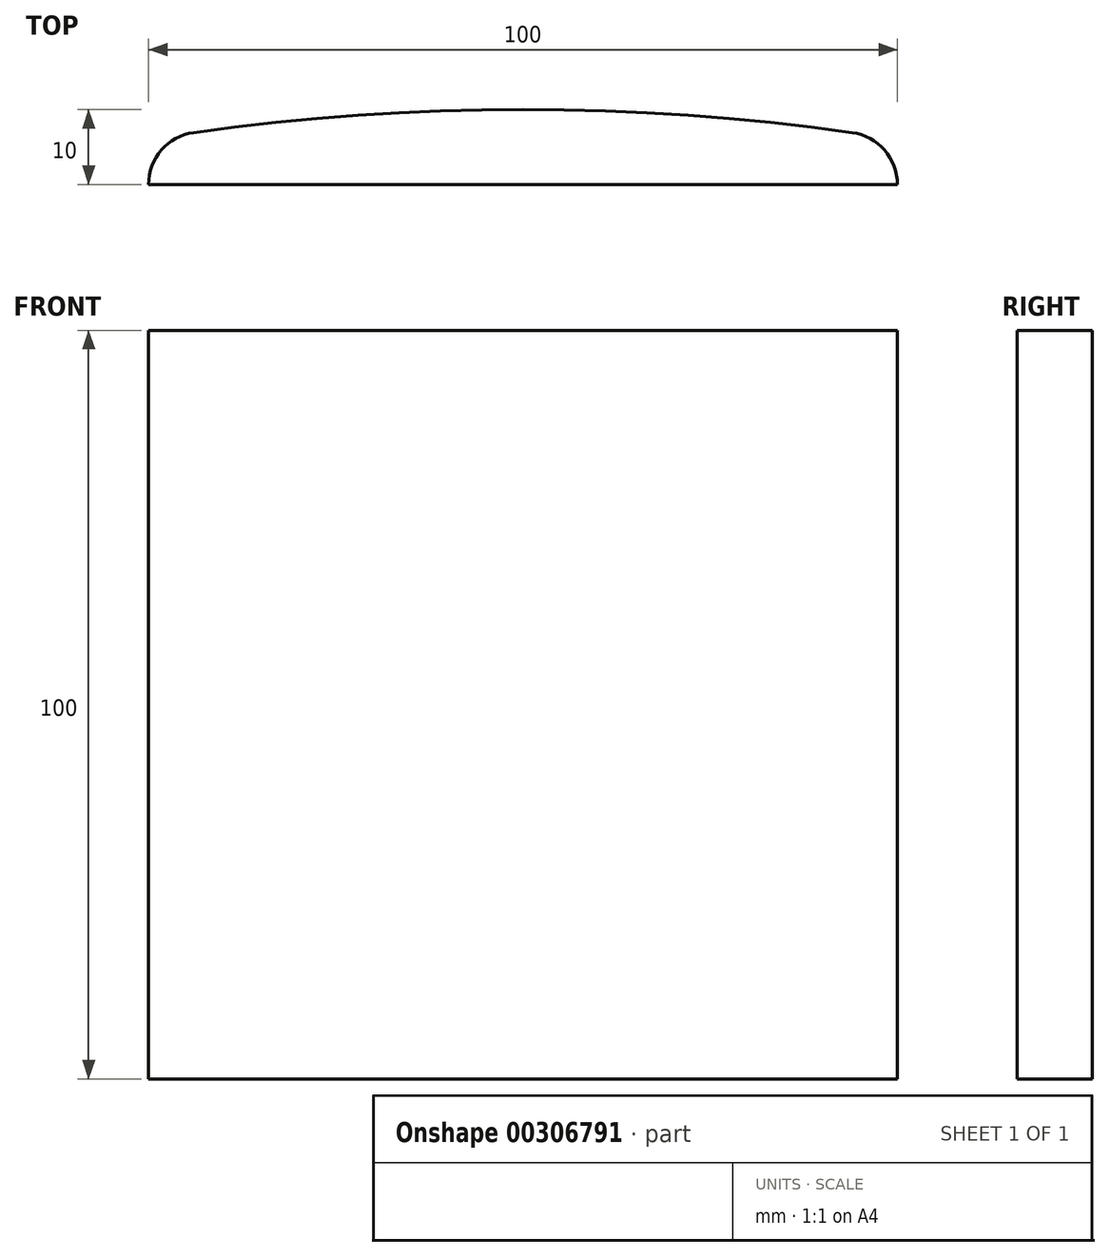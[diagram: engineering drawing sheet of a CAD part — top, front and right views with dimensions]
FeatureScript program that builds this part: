
annotation { "Feature Type Name" : "Feature", "Feature Type Description" : "" }
export const myFeature = defineFeature(function(context is Context, id is Id, definition is map)
    precondition{}
    {
        {
            var Q0;
            Q0=qCreatedBy(makeId("Top.planeOp"),FACE);
            var sketch = newSketch(context, id + "F0", { "sketchPlane" : qUnion([Q0])});
            skArc(sketch, "E0", {"start": v(100, 0) * mm, "mid": v(50, 2.63) * mm, "end": v(0, 0) * mm, "construction": true});
            skLineSegment(sketch, "E1.bottom", {"start": v(0, 0) * mm, "end": v(100, 0) * mm});
            skLineSegment(sketch, "E1.top", {"start": v(7, 7) * mm, "end": v(93, 7) * mm, "construction": true});
            skLineSegment(sketch, "E1.left", {"start": v(0, 0) * mm, "end": v(0, 0) * mm});
            skLineSegment(sketch, "E1.right", {"start": v(100, 0) * mm, "end": v(100, 0) * mm});
            skPoint(sketch, "E2.visualSharp", {"position": v(0, 7) * mm});
            skArc(sketch, "E2.filletArc", {"start": v(7, 7) * mm, "mid": v(2.05, 4.95) * mm, "end": v(0, 0) * mm});
            skPoint(sketch, "E3.visualSharp", {"position": v(100, 7) * mm});
            skArc(sketch, "E3.filletArc", {"start": v(100, 0) * mm, "mid": v(97.95, 4.95) * mm, "end": v(93, 7) * mm});
            skArc(sketch, "E4", {"start": v(93.97, 6.93) * mm, "mid": v(50, 10) * mm, "end": v(6.03, 6.93) * mm});
            skSolve(sketch);
        }
        {
            var Q0;
            {var subQ0=sQuery(id+"F0.wireOp",EDGE,"E1.bottom");Q0=makeQuery(id+"F0.imprint","IMPRINT",FACE,{"disambiguationData":[TD([[makeQuery(id+"F0.imprint","IMPRINT",EDGE,{"derivedFrom":subQ0}),1.0]])]});}
            extrude(context, id + "F1", {"entities" : qUnion([Q0]), "depth" : 100 * mm});
        }
    });
